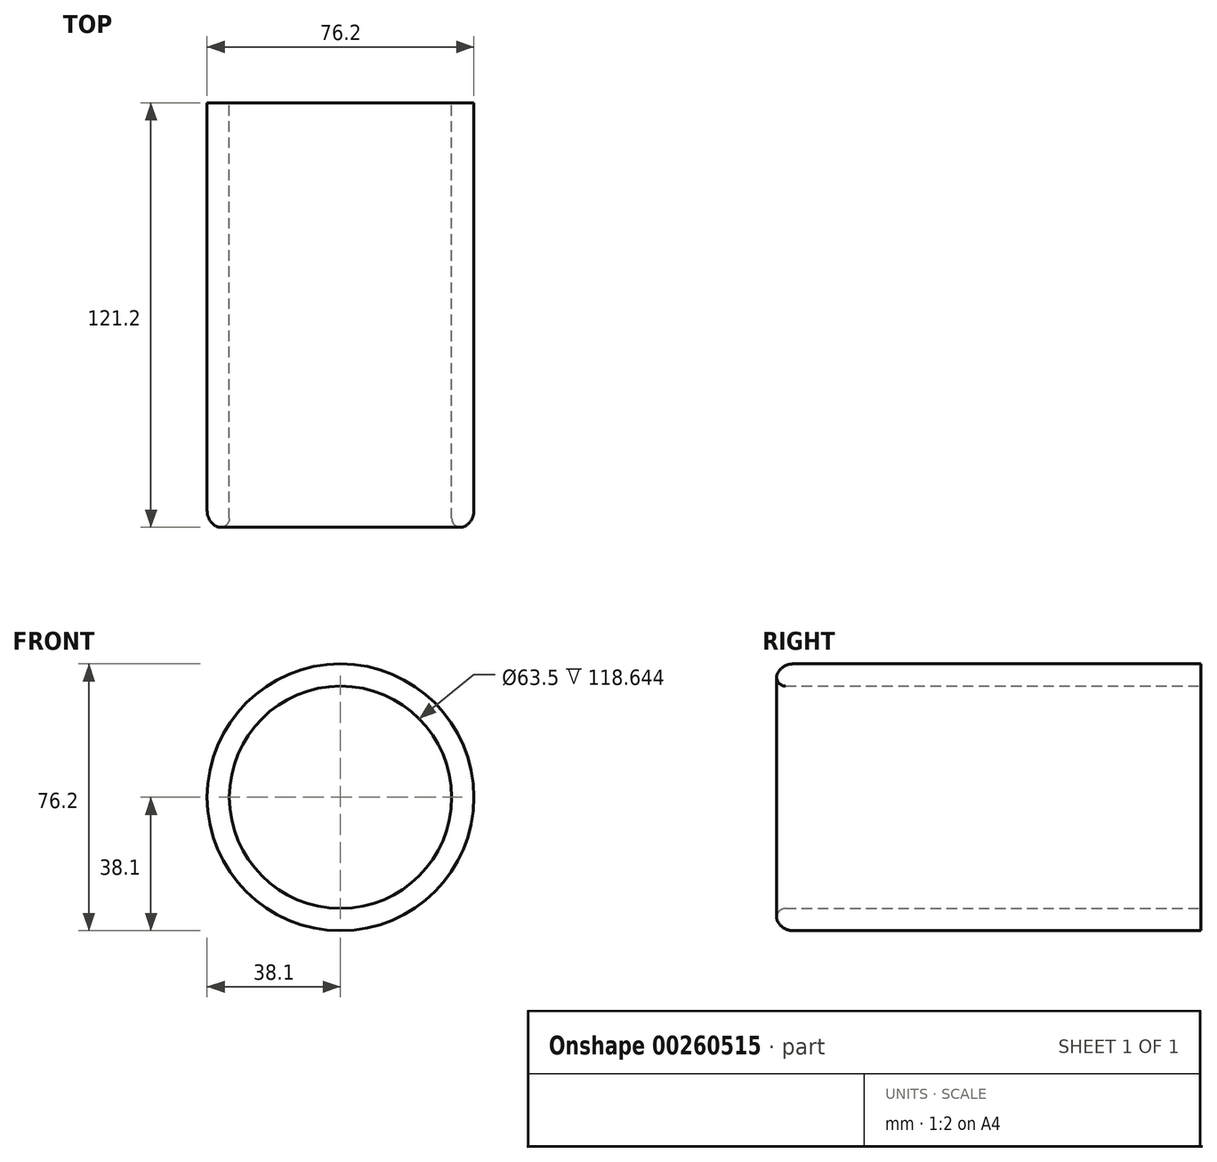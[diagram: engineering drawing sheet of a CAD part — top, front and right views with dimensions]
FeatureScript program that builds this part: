
annotation { "Feature Type Name" : "Feature", "Feature Type Description" : "" }
export const myFeature = defineFeature(function(context is Context, id is Id, definition is map)
    precondition{}
    {
        {
            var Q0;
            Q0=qCreatedBy(makeId("Front.planeOp"),FACE);
            var sketch = newSketch(context, id + "F0", { "sketchPlane" : qUnion([Q0])});
            skCircle(sketch, "E0", {"center": v(0, 0) * mm, "radius": 38.1 * mm});
            skLineSegment(sketch, "E1", {"start": v(38.1, 0) * mm, "end": v(31.75, 0) * mm});
            skCircle(sketch, "E2", {"center": v(0, 0) * mm, "radius": 31.75 * mm});
            skSolve(sketch);
        }
        {
            var Q0;
            Q0=makeQuery(id+"F0.imprint","IMPRINT",FACE,{"disambiguationData":[TD([[makeQuery(id+"F0.imprint","IMPRINT",EDGE,{"derivedFrom":sQuery(id+"F0.wireOp",EDGE,"E0")}),1.0]])]});
            extrude(context, id + "F1", {"entities" : qUnion([Q0]), "depth" : 121.54 * mm});
        }
        {
            var Q0;
            Q0=makeQuery(id+"F0.imprint","IMPRINT",FACE,{"disambiguationData":[TD([[makeQuery(id+"F0.imprint","IMPRINT",EDGE,{"derivedFrom":sQuery(id+"F0.wireOp",EDGE,"E2")}),1.0]])]});
            extrude(context, id + "F2", {"entities" : qUnion([Q0]), "operationType" : NewBodyOperationType.ADD, "depth" : 3 / 203.2 * mm});
        }
        {
            var Q0;
            Q0=makeQuery(id+"F1.opExtrude","CAP_EDGE",EDGE,{"disambiguationData":[OSD([sQuery(id+"F0.wireOp",EDGE,"E0")])],"isStart":false});
            fillet(context, id + "F3", {"entities" : qUnion([Q0]), "radius" : 5.08 * mm, "tangentPropagation" : true, "allowEdgeOverflow" : false});
        }
        {
            var Q0;
            Q0=makeQuery(id+"F1.opExtrude","CAP_EDGE",EDGE,{"disambiguationData":[OSD([sQuery(id+"F0.wireOp",EDGE,"E2")])],"isStart":false});
            fillet(context, id + "F4", {"entities" : qUnion([Q0]), "radius" : 2.54 * mm, "tangentPropagation" : true, "allowEdgeOverflow" : false});
        }
    });
